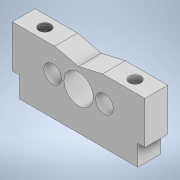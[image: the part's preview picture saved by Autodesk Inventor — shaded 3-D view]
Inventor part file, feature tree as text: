
AUTODESK INVENTOR PART (.ipt)
format: ipt  version: 2022 (Build 260153000, 153)  size: 155,648 bytes
history: native  units: mm
features: sketch x5, extrude x4, thread x1
ambient origin geometry x8: Origin, YZ Plane, XZ Plane, XY Plane, X Axis, Y Axis, Z Axis, Center Point
bodies: Solid1 (feature_tree)
feature tree (10):
  sketch  "Sketch1"  dims[d0=23.0mm d1=71.83mm]
  extrude  "Extrusion1"  Depth=71.83mm
  sketch  "Sketch3"  dims[d7=13.28mm d8=0.0mm]
  sketch  "Sketch4"  dims[d10=2.985766mm d11=35.915mm d12=15.875mm]
  extrude  "Extrusion2"  Depth=12.36mm
  extrude  "Extrusion3"  TaperAngle=0.0deg  [1 undecoded]
  extrude  "Extrusion4"  Depth=35.915mm
  thread  "Thread1"  [1 undecoded]
  sketch  "Sketch2"  dims[d2=12.36mm d3=0.0mm d4=25.88mm]
  sketch  "Sketch5"  dims[d13=9.5mm d14=14.0mm d15=9.5mm d16=9.5mm d17=14.0mm d18=9.525mm d19=9.525mm d20=64.14mm d21=11.25mm d22=3.845mm d23=0.0mm d24=12.36mm d25=0.0mm d26=12.36mm d27=0.0mm d28=6.18mm d29=6.35mm d30=11.4875mm d31=6.35mm d32=11.488mm d33=13.0mm d34=0.0mm d35=13.0mm d36=0.0mm]
note: 2 required parameter values undecoded (feature->parameter linkage not recoverable at this tier; creation-order binding heuristic only, values carry confidence <= 0.55)
